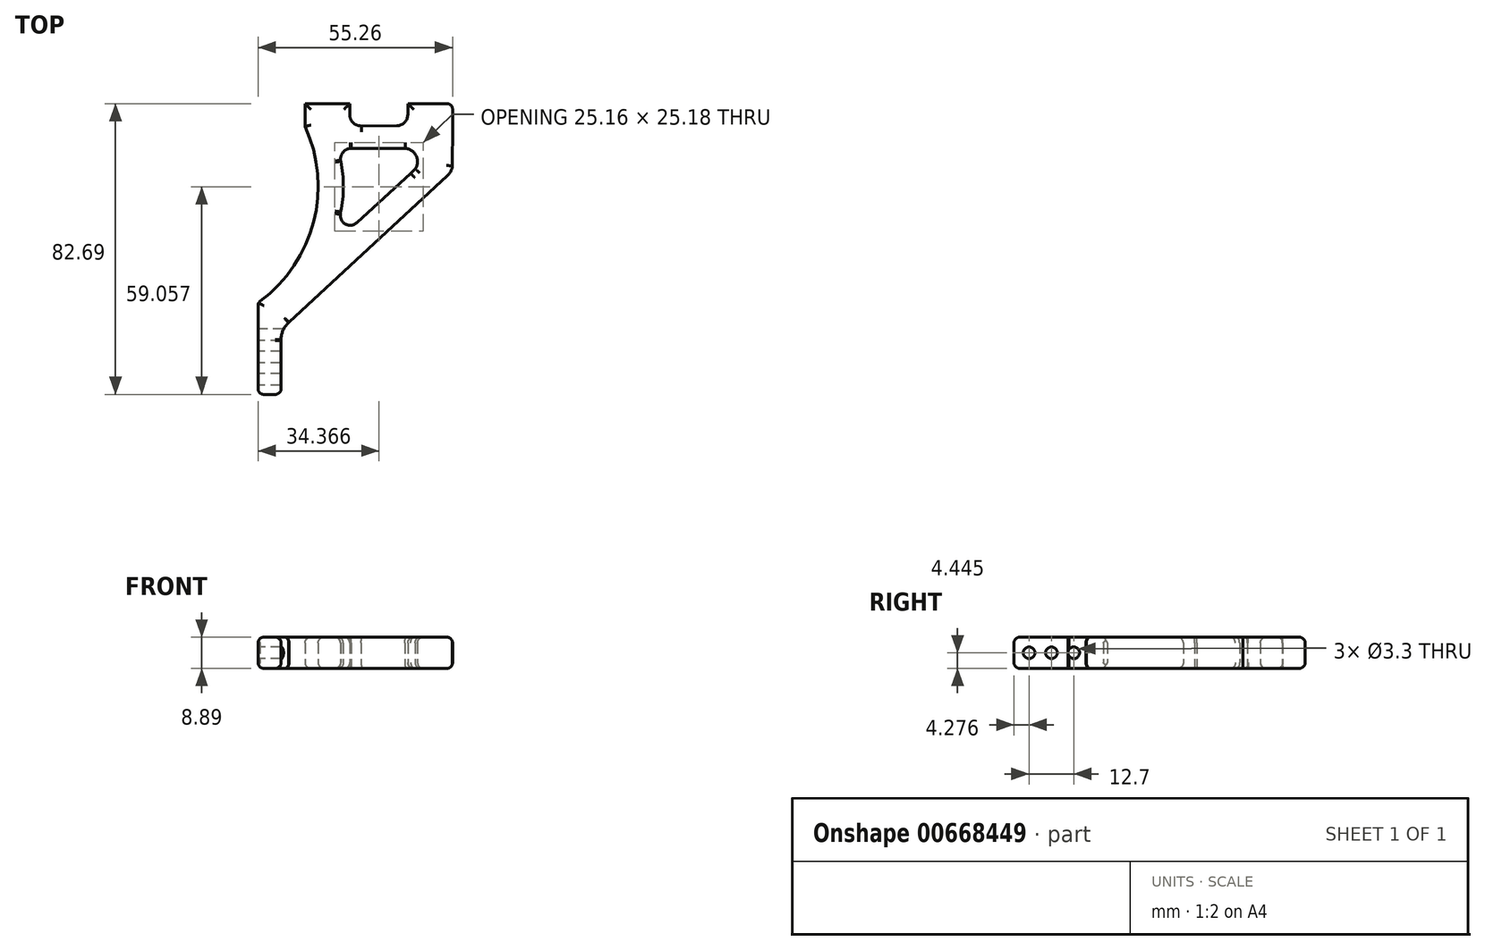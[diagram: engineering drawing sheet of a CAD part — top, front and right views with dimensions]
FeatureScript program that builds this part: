
annotation { "Feature Type Name" : "Feature", "Feature Type Description" : "" }
export const myFeature = defineFeature(function(context is Context, id is Id, definition is map)
    precondition{}
    {
        {
            var Q0;
            Q0=qCreatedBy(makeId("Top.planeOp"),FACE);
            var sketch = newSketch(context, id + "F0", { "sketchPlane" : qUnion([Q0])});
            skLineSegment(sketch, "E0.left", {"start": v(41.9, 22.85) * mm, "end": v(41.9, 16.36) * mm});
            skLineSegment(sketch, "E1.right", {"start": v(0, 22.82) * mm, "end": v(0, 16.36) * mm});
            skPoint(sketch, "E2", {"position": v(-13.35, -35.94) * mm});
            skLineSegment(sketch, "E3", {"start": v(30.03, 3.02) * mm, "end": v(31.32, 4.22) * mm});
            skArc(sketch, "E4", {"start": v(31.32, 4.22) * mm, "mid": v(31.58, 8.03) * mm, "end": v(28.41, 10.15) * mm});
            skArc(sketch, "E5", {"start": v(40.43, 2.3) * mm, "mid": v(41.62, 4.09) * mm, "end": v(41.88, 6.22) * mm});
            skLineSegment(sketch, "E6", {"start": v(41.9, 16.36) * mm, "end": v(41.88, 5.14) * mm});
            skLineSegment(sketch, "E7", {"start": v(40.43, 2.3) * mm, "end": v(-4.5, -39.3) * mm});
            skArc(sketch, "E8", {"start": v(26.03, 16.53) * mm, "mid": v(28.27, 17.46) * mm, "end": v(29.2, 19.7) * mm});
            skArc(sketch, "E9", {"start": v(12.72, 19.67) * mm, "mid": v(13.68, 17.4) * mm, "end": v(15.98, 16.5) * mm});
            skLineSegment(sketch, "E10", {"start": v(15.83, 16.5) * mm, "end": v(26.03, 16.53) * mm});
            skLineSegment(sketch, "E11", {"start": v(12.71, 22.85) * mm, "end": v(12.72, 19.67) * mm});
            skLineSegment(sketch, "E12", {"start": v(29.2, 22.85) * mm, "end": v(29.2, 19.7) * mm});
            skLineSegment(sketch, "E13", {"start": v(-6.79, -44.55) * mm, "end": v(-6.79, -58.18) * mm});
            skLineSegment(sketch, "E14", {"start": v(-8.44, -59.84) * mm, "end": v(-11.7, -59.84) * mm});
            skLineSegment(sketch, "E15", {"start": v(-13.35, -58.18) * mm, "end": v(-13.35, -34.41) * mm});
            skArc(sketch, "E16", {"start": v(-12.82, -33.37) * mm, "mid": v(2.45, -10.79) * mm, "end": v(0, 16.36) * mm});
            skPoint(sketch, "E17", {"position": v(6.3, 16.47) * mm});
            skArc(sketch, "E18", {"start": v(10.13, -7.94) * mm, "mid": v(10.89, -0.76) * mm, "end": v(10.14, 6.43) * mm});
            skLineSegment(sketch, "E19", {"start": v(28.41, 10.15) * mm, "end": v(13.18, 10.15) * mm});
            skArc(sketch, "E20", {"start": v(10.08, -8.6) * mm, "mid": v(11.55, -11.45) * mm, "end": v(14.72, -11.03) * mm});
            skLineSegment(sketch, "E21", {"start": v(30.03, 3.02) * mm, "end": v(14.72, -11.03) * mm});
            skLineSegment(sketch, "E22", {"start": v(10.13, -7.94) * mm, "end": v(10.08, -8.6) * mm});
            skArc(sketch, "E23", {"start": v(12.95, 10.13) * mm, "mid": v(10.81, 9.02) * mm, "end": v(10.11, 6.7) * mm});
            skLineSegment(sketch, "E24", {"start": v(10.1, 6.75) * mm, "end": v(10.14, 6.43) * mm});
            skLineSegment(sketch, "E25", {"start": v(13.18, 10.15) * mm, "end": v(12.95, 10.13) * mm});
            skArc(sketch, "E26", {"start": v(-4.62, -39.43) * mm, "mid": v(-6.25, -41.6) * mm, "end": v(-6.76, -44.28) * mm});
            skLineSegment(sketch, "E27", {"start": v(-4.5, -39.3) * mm, "end": v(-4.62, -39.43) * mm});
            skLineSegment(sketch, "E28", {"start": v(-6.79, -44.55) * mm, "end": v(-6.76, -44.28) * mm});
            skArc(sketch, "E29", {"start": v(-12.49, -33.12) * mm, "mid": v(-13.18, -33.85) * mm, "end": v(-13.35, -34.84) * mm});
            skPoint(sketch, "E30", {"position": v(3.18, 25.94) * mm});
            skPoint(sketch, "E31", {"position": v(9.55, 25.94) * mm});
            skPoint(sketch, "E32", {"position": v(32.36, 25.94) * mm});
            skPoint(sketch, "E33", {"position": v(38.73, 25.96) * mm});
            skPoint(sketch, "E34.visualSharp", {"position": v(-6.79, -59.84) * mm});
            skArc(sketch, "E34.filletArc", {"start": v(-8.44, -59.84) * mm, "mid": v(-7.27, -59.35) * mm, "end": v(-6.79, -58.18) * mm});
            skPoint(sketch, "E35.visualSharp", {"position": v(-13.35, -59.84) * mm});
            skArc(sketch, "E35.filletArc", {"start": v(-13.35, -58.18) * mm, "mid": v(-12.87, -59.35) * mm, "end": v(-11.7, -59.84) * mm});
            skLineSegment(sketch, "E36", {"start": v(0, 22.82) * mm, "end": v(12.71, 22.85) * mm});
            skLineSegment(sketch, "E37", {"start": v(29.2, 22.85) * mm, "end": v(41.9, 22.85) * mm});
            skSolve(sketch);
        }
        {
            var Q0;
            Q0=makeQuery(id+"F0.imprint","IMPRINT",FACE,{"disambiguationData":[TD([[makeQuery(id+"F0.imprint","IMPRINT",EDGE,{"derivedFrom":sQuery(id+"F0.wireOp",EDGE,"E0.left")}),-1.0]])]});
            extrude(context, id + "F1", {"entities" : qUnion([Q0]), "depth" : 8.9 * mm});
        }
        {
            var Q0;
            Q0=makeQuery(id+"F1.opExtrude","CAP_EDGE",EDGE,{"disambiguationData":[OSD([sQuery(id+"F0.wireOp",EDGE,"E0.left")])],"isStart":false});
            var Q1;
            Q1=makeQuery(id+"F1.opExtrude","CAP_FACE",FACE,{"disambiguationData":[OSD([sQuery(id+"F0.wireOp",EDGE,"YZ92rBNX-Mz95-2knB-doQ8-QHTFhwNA1oBr.bottom"),sQuery(id+"F0.wireOp",EDGE,"E0.bottom"),sQuery(id+"F0.wireOp",EDGE,"E0.left"),sQuery(id+"F0.wireOp",EDGE,"E1.right"),sQuery(id+"F0.wireOp",EDGE,"SzI1FcWJ-gVPU-Ooe5-hQlX-CRs42xu8LLNW"),sQuery(id+"F0.wireOp",EDGE,"TPr3rdG5-SIDz-w58Y-6eqx-M6IK6jSWFhIM"),sQuery(id+"F0.wireOp",EDGE,"noc51GMV-Ahoo-WSD5-Lxts-qJhaJEb6VlAm"),sQuery(id+"F0.wireOp",EDGE,"E3FnssW3-ZQiV-QDWY-5dQY-6bhZWmJ5cOBN"),sQuery(id+"F0.wireOp",EDGE,"cVz8xXeH-HXYV-y1n5-9CkQ-8dIsYkVWRJSO"),sQuery(id+"F0.wireOp",EDGE,"E3"),sQuery(id+"F0.wireOp",EDGE,"E4"),sQuery(id+"F0.wireOp",EDGE,"ISvdj8wT-oJ9k-pktH-wGl1-ypRnDfL9eN0U"),sQuery(id+"F0.wireOp",EDGE,"9vAMhoP7-wnIn-WaFN-PusH-oHm1aDkgCJVd"),sQuery(id+"F0.wireOp",EDGE,"Jhohd9hE-lPSl-7JDe-2Hk6-lUpt38s9H9Yq"),sQuery(id+"F0.wireOp",EDGE,"kMEoYta0-bXeg-MWsG-sC0e-sf47EgIndYf1"),sQuery(id+"F0.wireOp",EDGE,"G2y1UMqk-i9hO-i7C4-I75O-fc8mSGVlh6aF"),sQuery(id+"F0.wireOp",EDGE,"E5"),sQuery(id+"F0.wireOp",EDGE,"E6"),sQuery(id+"F0.wireOp",EDGE,"3kRvRCZS-lmxn-bb7c-7CfW-55qZRIPDTbnd"),sQuery(id+"F0.wireOp",EDGE,"iQ2rey6d-C9uf-Z5wj-gwGX-4HWEF9hhR8Rk"),sQuery(id+"F0.wireOp",EDGE,"E7"),sQuery(id+"F0.wireOp",EDGE,"EIM5bmiI-A2SF-qGVZ-bvCF-VrnpqsO6tJdX"),sQuery(id+"F0.wireOp",EDGE,"ilSpvZOG-ijNh-z112-y927-mz7fLowJOJxK"),sQuery(id+"F0.wireOp",EDGE,"El7EWY2H-2ioG-ogYt-Owtm-aVWLtx5Oh5om"),sQuery(id+"F0.wireOp",EDGE,"dyHQTCYp-uGCR-qaTb-hvYm-Fg8xv5Bd20ul"),sQuery(id+"F0.wireOp",EDGE,"kbVTQr7z-w13S-F5we-hJcG-RMuXYoLscjPo"),sQuery(id+"F0.wireOp",EDGE,"E8"),sQuery(id+"F0.wireOp",EDGE,"E9"),sQuery(id+"F0.wireOp",EDGE,"E10"),sQuery(id+"F0.wireOp",EDGE,"E11"),sQuery(id+"F0.wireOp",EDGE,"E12"),sQuery(id+"F0.wireOp",EDGE,"5bf2f562-2b39-48da-8c70-fd73b6cb9478.filletArc"),sQuery(id+"F0.wireOp",EDGE,"813d53ed-6ea3-4024-ad01-9081af5508ea.filletArc"),sQuery(id+"F0.wireOp",EDGE,"201358cc-a45b-47bb-b463-8872e7bce510.filletArc")])],"isStart":false});
            var Q2;
            Q2=makeQuery(id+"F1.opExtrude","CAP_FACE",FACE,{"disambiguationData":[OSD([sQuery(id+"F0.wireOp",EDGE,"YZ92rBNX-Mz95-2knB-doQ8-QHTFhwNA1oBr.bottom"),sQuery(id+"F0.wireOp",EDGE,"E0.bottom"),sQuery(id+"F0.wireOp",EDGE,"E0.left"),sQuery(id+"F0.wireOp",EDGE,"E1.right"),sQuery(id+"F0.wireOp",EDGE,"SzI1FcWJ-gVPU-Ooe5-hQlX-CRs42xu8LLNW"),sQuery(id+"F0.wireOp",EDGE,"TPr3rdG5-SIDz-w58Y-6eqx-M6IK6jSWFhIM"),sQuery(id+"F0.wireOp",EDGE,"noc51GMV-Ahoo-WSD5-Lxts-qJhaJEb6VlAm"),sQuery(id+"F0.wireOp",EDGE,"E3FnssW3-ZQiV-QDWY-5dQY-6bhZWmJ5cOBN"),sQuery(id+"F0.wireOp",EDGE,"cVz8xXeH-HXYV-y1n5-9CkQ-8dIsYkVWRJSO"),sQuery(id+"F0.wireOp",EDGE,"E3"),sQuery(id+"F0.wireOp",EDGE,"E4"),sQuery(id+"F0.wireOp",EDGE,"ISvdj8wT-oJ9k-pktH-wGl1-ypRnDfL9eN0U"),sQuery(id+"F0.wireOp",EDGE,"9vAMhoP7-wnIn-WaFN-PusH-oHm1aDkgCJVd"),sQuery(id+"F0.wireOp",EDGE,"Jhohd9hE-lPSl-7JDe-2Hk6-lUpt38s9H9Yq"),sQuery(id+"F0.wireOp",EDGE,"kMEoYta0-bXeg-MWsG-sC0e-sf47EgIndYf1"),sQuery(id+"F0.wireOp",EDGE,"G2y1UMqk-i9hO-i7C4-I75O-fc8mSGVlh6aF"),sQuery(id+"F0.wireOp",EDGE,"E5"),sQuery(id+"F0.wireOp",EDGE,"E6"),sQuery(id+"F0.wireOp",EDGE,"3kRvRCZS-lmxn-bb7c-7CfW-55qZRIPDTbnd"),sQuery(id+"F0.wireOp",EDGE,"iQ2rey6d-C9uf-Z5wj-gwGX-4HWEF9hhR8Rk"),sQuery(id+"F0.wireOp",EDGE,"E7"),sQuery(id+"F0.wireOp",EDGE,"EIM5bmiI-A2SF-qGVZ-bvCF-VrnpqsO6tJdX"),sQuery(id+"F0.wireOp",EDGE,"ilSpvZOG-ijNh-z112-y927-mz7fLowJOJxK"),sQuery(id+"F0.wireOp",EDGE,"El7EWY2H-2ioG-ogYt-Owtm-aVWLtx5Oh5om"),sQuery(id+"F0.wireOp",EDGE,"dyHQTCYp-uGCR-qaTb-hvYm-Fg8xv5Bd20ul"),sQuery(id+"F0.wireOp",EDGE,"kbVTQr7z-w13S-F5we-hJcG-RMuXYoLscjPo"),sQuery(id+"F0.wireOp",EDGE,"E8"),sQuery(id+"F0.wireOp",EDGE,"E9"),sQuery(id+"F0.wireOp",EDGE,"E10"),sQuery(id+"F0.wireOp",EDGE,"E11"),sQuery(id+"F0.wireOp",EDGE,"E12"),sQuery(id+"F0.wireOp",EDGE,"5bf2f562-2b39-48da-8c70-fd73b6cb9478.filletArc"),sQuery(id+"F0.wireOp",EDGE,"813d53ed-6ea3-4024-ad01-9081af5508ea.filletArc"),sQuery(id+"F0.wireOp",EDGE,"201358cc-a45b-47bb-b463-8872e7bce510.filletArc")])],"isStart":true});
            var Q3;
            Q3=makeQuery(id+"F1.opExtrude","SWEPT_EDGE",EDGE,{"disambiguationData":[OSD([sQuery(id+"F0.wireOp",EDGE,"E0.bottom"),sQuery(id+"F0.wireOp",EDGE,"E0.left")])]});
            var Q4;
            Q4=makeQuery(id+"F1.opExtrude","SWEPT_EDGE",EDGE,{"disambiguationData":[OSD([sQuery(id+"F0.wireOp",EDGE,"noc51GMV-Ahoo-WSD5-Lxts-qJhaJEb6VlAm"),sQuery(id+"F0.wireOp",EDGE,"E3FnssW3-ZQiV-QDWY-5dQY-6bhZWmJ5cOBN")])]});
            var Q5;
            Q5=makeQuery(id+"F1.opExtrude","SWEPT_EDGE",EDGE,{"disambiguationData":[OSD([sQuery(id+"F0.wireOp",EDGE,"TPr3rdG5-SIDz-w58Y-6eqx-M6IK6jSWFhIM"),sQuery(id+"F0.wireOp",EDGE,"noc51GMV-Ahoo-WSD5-Lxts-qJhaJEb6VlAm")])]});
            fillet(context, id + "F2", {"entities" : qUnion([Q0, Q1, Q2, Q3, Q4, Q5]), "radius" : 1.65 * mm, "tangentPropagation" : true, "allowEdgeOverflow" : false});
        }
        {
            var Q0;
            Q0=makeQuery(id+"F1.opExtrude","SWEPT_FACE",FACE,{"disambiguationData":[OSD([sQuery(id+"F0.wireOp",EDGE,"E15")])]});
            var sketch = newSketch(context, id + "F3", { "sketchPlane" : qUnion([Q0])});
            skPoint(sketch, "E38", {"position": v(46.3, 7.24) * mm});
            skPoint(sketch, "E39", {"position": v(46.3, 1.65) * mm});
            skPoint(sketch, "E40", {"position": v(58.18, 4.45) * mm});
            skPoint(sketch, "E41", {"position": v(34.41, 4.45) * mm});
            skCircle(sketch, "E42", {"center": v(55.56, 4.45) * mm, "radius": 2.2 * mm});
            skPoint(sketch, "E43.orphan", {"position": v(34.41, 1.65) * mm});
            skPoint(sketch, "E44.orphan", {"position": v(58.18, 1.65) * mm});
            skLineSegment(sketch, "E45", {"start": v(58.18, 4.45) * mm, "end": v(34.41, 4.45) * mm});
            skCircle(sketch, "E46", {"center": v(42.86, 4.45) * mm, "radius": 2.15 * mm});
            skCircle(sketch, "E47", {"center": v(49.21, 4.45) * mm, "radius": 2.1 * mm});
            skSolve(sketch);
        }
        {
            var Q0;
            Q0=sQuery(id+"F3.wireOp",VERTEX,"E42.center");
            var Q1;
            Q1=sQuery(id+"F3.wireOp",VERTEX,"E47.center");
            var Q2;
            Q2=sQuery(id+"F3.wireOp",VERTEX,"E46.center");
            var Q3;
            Q3=makeQuery(id+"F1.opExtrude","SWEPT_BODY",BODY,{"disambiguationData":[OSD([sQuery(id+"F0.wireOp",EDGE,"E0.left"),sQuery(id+"F0.wireOp",EDGE,"E1.right"),sQuery(id+"F0.wireOp",EDGE,"E3"),sQuery(id+"F0.wireOp",EDGE,"E4"),sQuery(id+"F0.wireOp",EDGE,"E5"),sQuery(id+"F0.wireOp",EDGE,"E6"),sQuery(id+"F0.wireOp",EDGE,"E7"),sQuery(id+"F0.wireOp",EDGE,"E8"),sQuery(id+"F0.wireOp",EDGE,"E9"),sQuery(id+"F0.wireOp",EDGE,"E10"),sQuery(id+"F0.wireOp",EDGE,"E11"),sQuery(id+"F0.wireOp",EDGE,"E12"),sQuery(id+"F0.wireOp",EDGE,"E13"),sQuery(id+"F0.wireOp",EDGE,"E14"),sQuery(id+"F0.wireOp",EDGE,"E15"),sQuery(id+"F0.wireOp",EDGE,"E16"),sQuery(id+"F0.wireOp",EDGE,"E18"),sQuery(id+"F0.wireOp",EDGE,"E19"),sQuery(id+"F0.wireOp",EDGE,"E20"),sQuery(id+"F0.wireOp",EDGE,"E21"),sQuery(id+"F0.wireOp",EDGE,"E22"),sQuery(id+"F0.wireOp",EDGE,"E23"),sQuery(id+"F0.wireOp",EDGE,"E24"),sQuery(id+"F0.wireOp",EDGE,"E25"),sQuery(id+"F0.wireOp",EDGE,"E26"),sQuery(id+"F0.wireOp",EDGE,"E27"),sQuery(id+"F0.wireOp",EDGE,"E28"),sQuery(id+"F0.wireOp",EDGE,"E29"),sQuery(id+"F0.wireOp",EDGE,"181tW4vp-ZbtW-davR-69ns-0IIxqZoocxi7"),sQuery(id+"F0.wireOp",EDGE,"CLDTVJRU-Zfvq-rIZ4-dqXF-aQIPlVdSOrB2"),sQuery(id+"F0.wireOp",EDGE,"2JWichqw-htUA-xdmc-76uD-T1Hjylxb60dA"),sQuery(id+"F0.wireOp",EDGE,"FRX9JyIv-8L25-IehD-1VqH-pjbuIYerUjMn"),sQuery(id+"F0.wireOp",EDGE,"0ZqjfKFE-V8Ua-lY5Q-Bvau-9FpRgLLehYvd"),sQuery(id+"F0.wireOp",EDGE,"Xe9JL77E-bn8W-FsuT-8ZNO-0icE26lyWPuJ"),sQuery(id+"F0.wireOp",EDGE,"E34.filletArc"),sQuery(id+"F0.wireOp",EDGE,"E35.filletArc")])]});
            hole(context, id + "F4", {"style" : HoleStyle.SIMPLE, "endStyle" : HoleEndStyle.THROUGH, "standardTappedOrClearance" : lookupTablePath({ "standard" : "ISO", "fit" : "Normal", "size" : "M3", "type" : "Clearance" }), "standardBlindInLast" : lookupTablePath({ "fit" : "Standard", "standard" : "ISO", "size" : "M3", "type" : "Clearance" }), "holeDiameter" : 3.3 * mm, "isTappedThrough" : true, "tappedDepth" : 12.7 * mm, "tapClearance" : 3, "locations" : qUnion([Q0, Q1, Q2]), "scope" : qUnion([Q3])});
        }
    });
